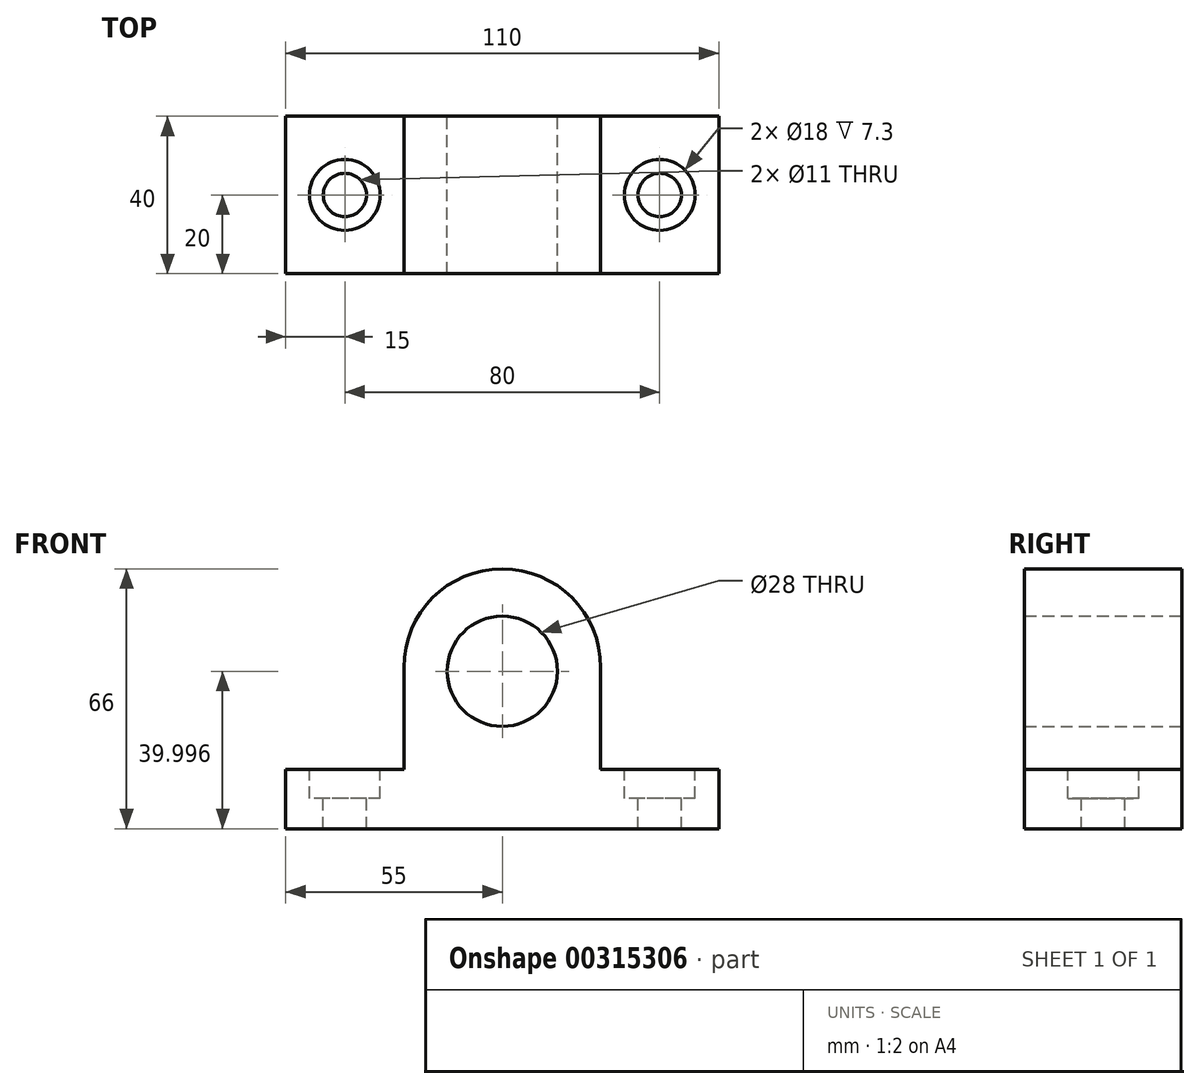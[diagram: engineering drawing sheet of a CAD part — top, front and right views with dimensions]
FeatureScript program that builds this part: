
annotation { "Feature Type Name" : "Feature", "Feature Type Description" : "" }
export const myFeature = defineFeature(function(context is Context, id is Id, definition is map)
    precondition{}
    {
        {
            var Q0;
            Q0=qCreatedBy(makeId("Front.planeOp"),FACE);
            var sketch = newSketch(context, id + "F0", { "sketchPlane" : qUnion([Q0])});
            skLineSegment(sketch, "E0", {"start": v(-45.14, -10.73) * mm, "end": v(-45.14, -25.73) * mm});
            skLineSegment(sketch, "E1", {"start": v(-45.14, -25.73) * mm, "end": v(64.86, -25.73) * mm});
            skLineSegment(sketch, "E2", {"start": v(64.86, -25.73) * mm, "end": v(64.86, -10.73) * mm});
            skLineSegment(sketch, "E3", {"start": v(64.86, -10.73) * mm, "end": v(34.86, -10.73) * mm});
            skLineSegment(sketch, "E4", {"start": v(34.86, -10.73) * mm, "end": v(34.86, 15.27) * mm});
            skLineSegment(sketch, "E5", {"start": v(-15.14, -10.73) * mm, "end": v(-45.14, -10.73) * mm});
            skLineSegment(sketch, "E6", {"start": v(-15.14, 15.27) * mm, "end": v(-15.14, -10.73) * mm});
            skCircle(sketch, "E7", {"center": v(9.86, 14.27) * mm, "radius": 14 * mm});
            skArc(sketch, "E8", {"start": v(34.86, 15.27) * mm, "mid": v(9.86, 40.27) * mm, "end": v(-15.14, 15.27) * mm});
            skSolve(sketch);
        }
        {
            var Q0;
            Q0=makeQuery(id+"F0.imprint","IMPRINT",FACE,{"disambiguationData":[TD([[makeQuery(id+"F0.imprint","IMPRINT",EDGE,{"derivedFrom":sQuery(id+"F0.wireOp",EDGE,"E0")}),1.0]])]});
            extrude(context, id + "F1", {"entities" : qUnion([Q0]), "depth" : 40 * mm});
        }
        {
            var Q0;
            Q0=makeQuery(id+"F1.opExtrude","SWEPT_FACE",FACE,{"disambiguationData":[OSD([sQuery(id+"F0.wireOp",EDGE,"E5")])]});
            var sketch = newSketch(context, id + "F2", { "sketchPlane" : qUnion([Q0])});
            skCircle(sketch, "E9", {"center": v(-30.14, -20) * mm, "radius": 9 * mm});
            skCircle(sketch, "E10", {"center": v(49.86, -20) * mm, "radius": 9 * mm});
            skSolve(sketch);
        }
        {
            var Q0;
            Q0=makeQuery(id+"F2.imprint","IMPRINT",FACE,{"disambiguationData":[TD([[makeQuery(id+"F2.imprint","IMPRINT",EDGE,{"derivedFrom":sQuery(id+"F2.wireOp",EDGE,"E9")}),1.0]])]});
            var Q1;
            Q1=makeQuery(id+"F2.imprint","IMPRINT",FACE,{"disambiguationData":[TD([[makeQuery(id+"F2.imprint","IMPRINT",EDGE,{"derivedFrom":sQuery(id+"F2.wireOp",EDGE,"E10")}),1.0]])]});
            extrude(context, id + "F3", {"entities" : qUnion([Q0, Q1]), "operationType" : NewBodyOperationType.REMOVE, "oppositeDirection" : true, "depth" : 7.3 * mm});
        }
        {
            var Q0;
            Q0=makeQuery(id+"F3.boolean.opBoolean","COPY",FACE,{"derivedFrom":makeQuery(id+"F3.opExtrude","CAP_FACE",FACE,{"disambiguationData":[OSD([sQuery(id+"F2.wireOp",EDGE,"E9")])],"isStart":false})});
            var sketch = newSketch(context, id + "F4", { "sketchPlane" : qUnion([Q0])});
            skCircle(sketch, "E11", {"center": v(-30.14, -20) * mm, "radius": 5.5 * mm});
            skSolve(sketch);
        }
        {
            var Q0;
            Q0=makeQuery(id+"F3.boolean.opBoolean","COPY",FACE,{"derivedFrom":makeQuery(id+"F3.opExtrude","CAP_FACE",FACE,{"disambiguationData":[OSD([sQuery(id+"F2.wireOp",EDGE,"E10")])],"isStart":false})});
            var sketch = newSketch(context, id + "F5", { "sketchPlane" : qUnion([Q0])});
            skCircle(sketch, "E12", {"center": v(49.86, -20) * mm, "radius": 5.5 * mm});
            skSolve(sketch);
        }
        {
            var Q0;
            Q0=makeQuery(id+"F4.imprint","IMPRINT",FACE,{"disambiguationData":[TD([[makeQuery(id+"F4.imprint","IMPRINT",EDGE,{"derivedFrom":sQuery(id+"F4.wireOp",EDGE,"E11")}),1.0]])]});
            var Q1;
            Q1=makeQuery(id+"F5.imprint","IMPRINT",FACE,{"disambiguationData":[TD([[makeQuery(id+"F5.imprint","IMPRINT",EDGE,{"derivedFrom":sQuery(id+"F5.wireOp",EDGE,"E12")}),1.0]])]});
            extrude(context, id + "F6", {"entities" : qUnion([Q0, Q1]), "operationType" : NewBodyOperationType.REMOVE, "oppositeDirection" : true, "depth" : 25 * mm});
        }
    });
